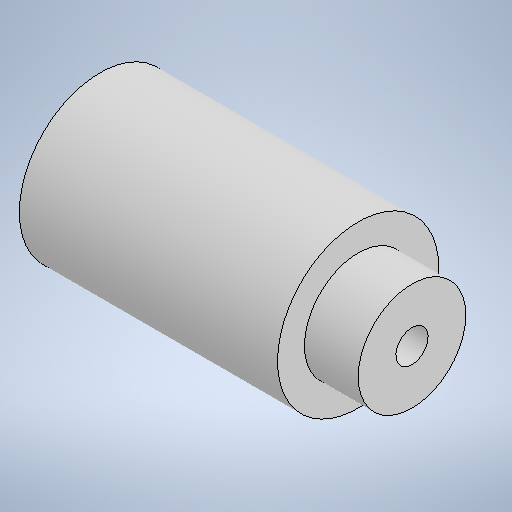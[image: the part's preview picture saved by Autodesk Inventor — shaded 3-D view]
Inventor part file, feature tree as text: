
AUTODESK INVENTOR PART (.ipt)
format: ipt  version: 2025 (Build 290162010, 162A)  size: 231,424 bytes
history: native  units: mm
features: sketch x2, revolve x1, hole x1, thread x1
ambient origin geometry x8: Origin, YZ Plane, XZ Plane, XY Plane, X Axis, Y Axis, Z Axis, Center Point
bodies: Solid1 (feature_tree)
feature tree (5):
  revolve  "Revolution1"  [1 undecoded]
  hole  "Hole1"  [1 undecoded]
  thread  "Thread1"  [1 undecoded]
  sketch  "Sketch1"  dims[d0=24.0mm d1=5.0mm]
  sketch  "Sketch2"  dims[d2=15.0mm d3=10.0mm d4=90.0deg d5=3.0mm d6=16.0mm d7=8.0mm d8=18.0mm d9=90.0deg d10=29.0mm d11=0.0mm d12=18.0mm d13=0.0mm]
note: 3 required parameter values undecoded (feature->parameter linkage not recoverable at this tier; creation-order binding heuristic only, values carry confidence <= 0.55)